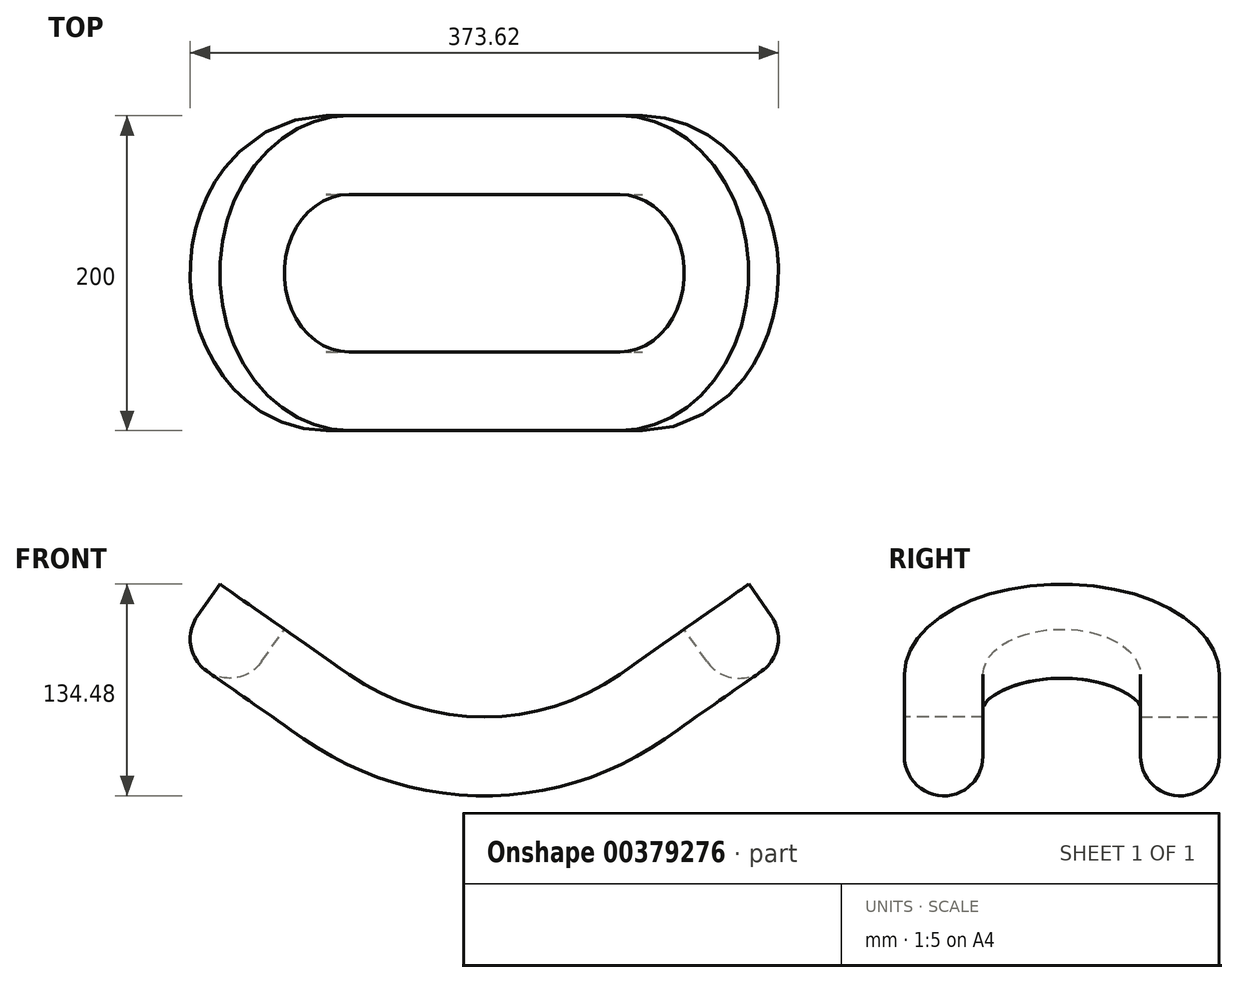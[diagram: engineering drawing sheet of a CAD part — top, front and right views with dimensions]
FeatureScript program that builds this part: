
annotation { "Feature Type Name" : "Feature", "Feature Type Description" : "" }
export const myFeature = defineFeature(function(context is Context, id is Id, definition is map)
    precondition{}
    {
        {
            var Q0;
            Q0=qCreatedBy(makeId("Front.planeOp"),FACE);
            var sketch = newSketch(context, id + "F0", { "sketchPlane" : qUnion([Q0])});
            skArc(sketch, "E0", {"start": v(114.72, 36.17) * mm, "mid": v(60.14, 9.26) * mm, "end": v(0, 0) * mm});
            skLineSegment(sketch, "E1", {"start": v(114.72, 36.17) * mm, "end": v(196.63, 93.53) * mm});
            skLineSegment(sketch, "E2", {"start": v(0, 200) * mm, "end": v(114.72, 36.17) * mm, "construction": true});
            skLineSegment(sketch, "E3", {"start": v(0, 200) * mm, "end": v(0, 0) * mm, "construction": true});
            skSolve(sketch);
        }
        {
            var Q0;
            Q0=sQuery(id+"F0.wireOp",EDGE,"E1");
            var Q1;
            Q1=sQuery(id+"F0.wireOp",EDGE,"E0");
            extrude(context, id + "F1", {"bodyType" : ToolBodyType.SURFACE, "surfaceEntities" : qUnion([Q0, Q1]), "depth" : 100 * mm});
        }
        {
            var Q0;
            Q0=makeQuery(id+"F1.opExtrude","SWEPT_FACE",FACE,{"disambiguationData":[OSD([sQuery(id+"F0.wireOp",EDGE,"E1")])]});
            var sketch = newSketch(context, id + "F2", { "sketchPlane" : qUnion([Q0])});
            skArc(sketch, "E4", {"start": v(214.72, 0) * mm, "mid": v(185.43, 70.71) * mm, "end": v(114.72, 100) * mm});
            skSolve(sketch);
        }
        {
            var Q0;
            Q0=qCreatedBy(makeId("Right.planeOp"),FACE);
            var sketch = newSketch(context, id + "F3", { "sketchPlane" : qUnion([Q0])});
            skLineSegment(sketch, "E5.bottom", {"start": v(-50, 50) * mm, "end": v(-100, 50) * mm});
            skLineSegment(sketch, "E5.top", {"start": v(-50, 25) * mm, "end": v(-100, 25) * mm, "construction": true});
            skLineSegment(sketch, "E5.left", {"start": v(-50, 50) * mm, "end": v(-50, 25) * mm});
            skLineSegment(sketch, "E5.right", {"start": v(-100, 50) * mm, "end": v(-100, 25) * mm});
            skArc(sketch, "E6", {"start": v(-50, 25) * mm, "mid": v(-75, 0) * mm, "end": v(-100, 25) * mm});
            skSolve(sketch);
        }
        {
            var Q0;
            Q0=makeQuery(id+"F3.imprint","IMPRINT",FACE,{"disambiguationData":[TD([[makeQuery(id+"F3.imprint","IMPRINT",EDGE,{"derivedFrom":sQuery(id+"F3.wireOp",EDGE,"E5.bottom")}),1.0]])]});
            var Q1;
            Q1=makeQuery(id+"F1.opExtrude","CAP_EDGE",EDGE,{"disambiguationData":[OSD([sQuery(id+"F0.wireOp",EDGE,"E0")])],"isStart":false});
            var Q2;
            Q2=sQuery(id+"F2.wireOp",EDGE,"E4");
            sweep(context, id + "F4", {"profiles" : qUnion([Q0]), "path" : qUnion([Q1, Q2])});
        }
        {
            var Q0;
            Q0=makeQuery(id+"F4.opSweep","SWEPT_BODY",BODY,{"disambiguationData":[OSD([sQuery(id+"F2.wireOp",EDGE,"E4"),sQuery(id+"F3.wireOp",EDGE,"E5.bottom"),sQuery(id+"F3.wireOp",EDGE,"E5.left"),sQuery(id+"F3.wireOp",EDGE,"E5.right"),sQuery(id+"F3.wireOp",EDGE,"E6")])]});
            var Q1;
            Q1=qCreatedBy(makeId("Front.planeOp"),FACE);
            mirror(context, id + "F5", {"operationType" : NewBodyOperationType.ADD, "entities" : qUnion([Q0]), "mirrorPlane" : qUnion([Q1])});
        }
        {
            var Q0;
            Q0=makeQuery(id+"F4.opSweep","SWEPT_BODY",BODY,{"disambiguationData":[OSD([sQuery(id+"F2.wireOp",EDGE,"E4"),sQuery(id+"F3.wireOp",EDGE,"E5.bottom"),sQuery(id+"F3.wireOp",EDGE,"E5.left"),sQuery(id+"F3.wireOp",EDGE,"E5.right"),sQuery(id+"F3.wireOp",EDGE,"E6")])]});
            var Q1;
            Q1=qCreatedBy(makeId("Right.planeOp"),FACE);
            mirror(context, id + "F6", {"operationType" : NewBodyOperationType.ADD, "entities" : qUnion([Q0]), "mirrorPlane" : qUnion([Q1])});
        }
    });
